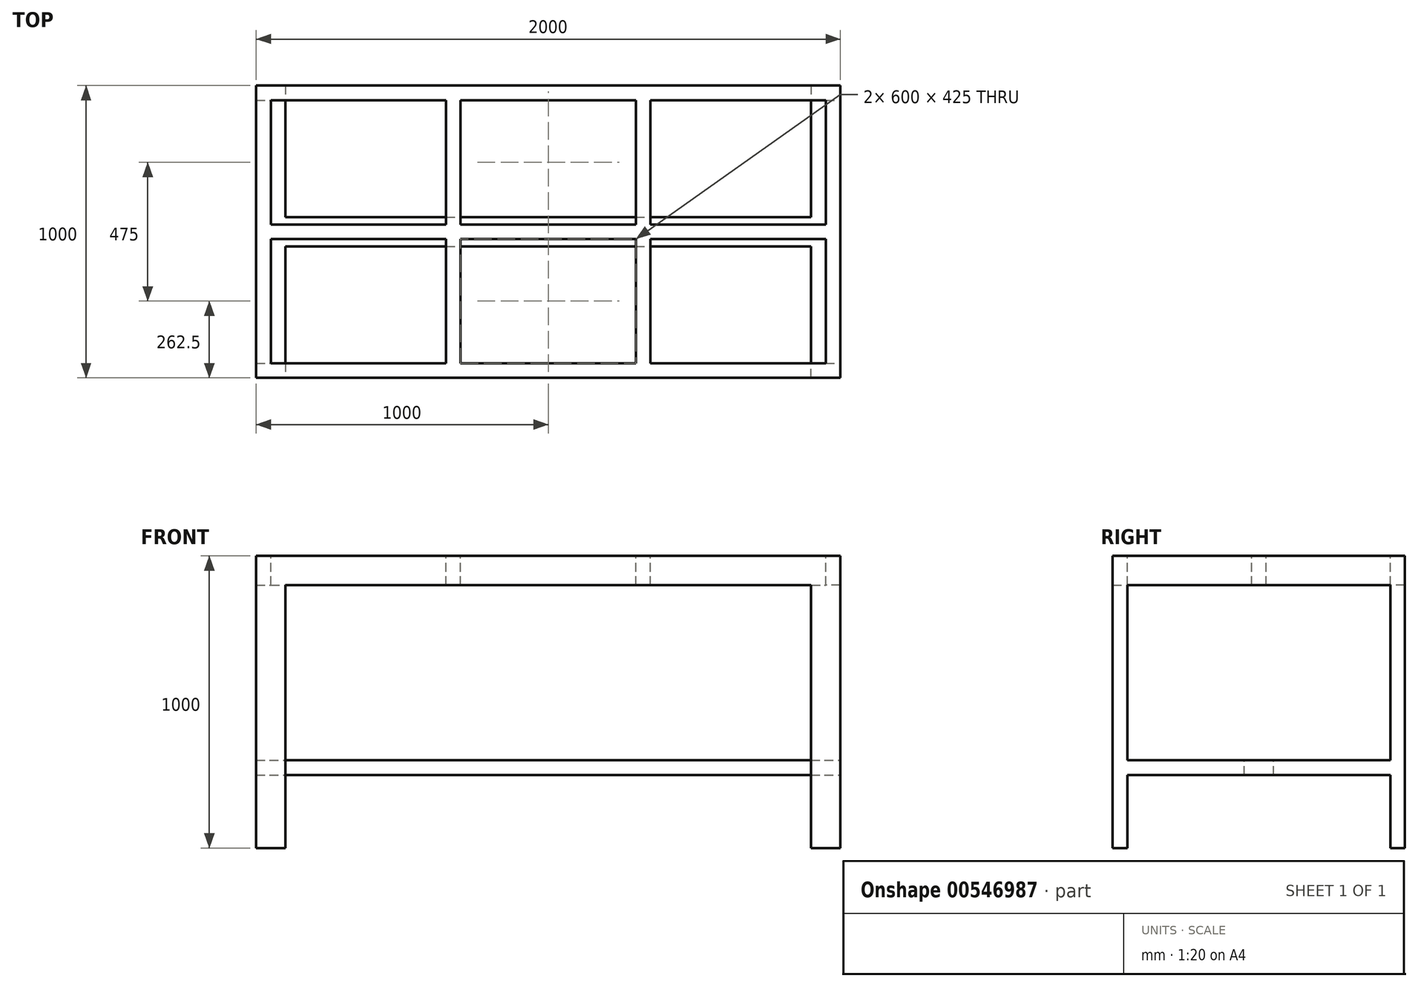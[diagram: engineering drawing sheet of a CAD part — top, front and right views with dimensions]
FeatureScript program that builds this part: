
annotation { "Feature Type Name" : "Feature", "Feature Type Description" : "" }
export const myFeature = defineFeature(function(context is Context, id is Id, definition is map)
    precondition{}
    {
        {
            var Q0;
            Q0=qCreatedBy(makeId("Top.planeOp"),FACE);
            var sketch = newSketch(context, id + "F0", { "sketchPlane" : qUnion([Q0])});
            skLineSegment(sketch, "E0.bottom", {"start": v(-989.4, 627.58) * mm, "end": v(1010.6, 627.58) * mm});
            skLineSegment(sketch, "E0.top", {"start": v(-989.4, -372.42) * mm, "end": v(1010.6, -372.42) * mm});
            skLineSegment(sketch, "E0.left", {"start": v(-989.4, 627.58) * mm, "end": v(-989.4, -372.42) * mm});
            skLineSegment(sketch, "E0.right", {"start": v(1010.6, 627.58) * mm, "end": v(1010.6, -372.42) * mm});
            skSolve(sketch);
        }
        {
            var Q0;
            Q0=makeQuery(id+"F0.imprint","IMPRINT",FACE,{"disambiguationData":[TD([[makeQuery(id+"F0.imprint","IMPRINT",EDGE,{"derivedFrom":sQuery(id+"F0.wireOp",EDGE,"E0.bottom")}),-1.0]])]});
            extrude(context, id + "F1", {"entities" : qUnion([Q0]), "depth" : 100 * mm, "offsetDistance" : 25 * mm});
        }
        {
            var Q0;
            Q0=makeQuery(id+"F1.opExtrude","CAP_FACE",FACE,{"disambiguationData":[OSD([sQuery(id+"F0.wireOp",EDGE,"E0.bottom"),sQuery(id+"F0.wireOp",EDGE,"E0.top"),sQuery(id+"F0.wireOp",EDGE,"E0.left"),sQuery(id+"F0.wireOp",EDGE,"E0.right")])],"isStart":false});
            var sketch = newSketch(context, id + "F2", { "sketchPlane" : qUnion([Q0])});
            skLineSegment(sketch, "E1.bottom", {"start": v(-939.4, 577.58) * mm, "end": v(-339.4, 577.58) * mm});
            skLineSegment(sketch, "E1.top", {"start": v(-939.4, 152.58) * mm, "end": v(-339.4, 152.58) * mm});
            skLineSegment(sketch, "E1.left", {"start": v(-939.4, 577.58) * mm, "end": v(-939.4, 152.58) * mm});
            skLineSegment(sketch, "E1.right", {"start": v(-339.4, 577.58) * mm, "end": v(-339.4, 152.58) * mm});
            skLineSegment(sketch, "E2.bottom", {"start": v(-939.4, 102.58) * mm, "end": v(-339.4, 102.58) * mm});
            skLineSegment(sketch, "E2.top", {"start": v(-939.4, -322.42) * mm, "end": v(-339.4, -322.42) * mm});
            skLineSegment(sketch, "E2.left", {"start": v(-939.4, 102.58) * mm, "end": v(-939.4, -322.42) * mm});
            skLineSegment(sketch, "E2.right", {"start": v(-339.4, 102.58) * mm, "end": v(-339.4, -322.42) * mm});
            skLineSegment(sketch, "E3.bottom", {"start": v(-289.4, 577.58) * mm, "end": v(310.6, 577.58) * mm});
            skLineSegment(sketch, "E3.top", {"start": v(-289.4, 152.58) * mm, "end": v(310.6, 152.58) * mm});
            skLineSegment(sketch, "E3.left", {"start": v(-289.4, 577.58) * mm, "end": v(-289.4, 152.58) * mm});
            skLineSegment(sketch, "E3.right", {"start": v(310.6, 577.58) * mm, "end": v(310.6, 152.58) * mm});
            skLineSegment(sketch, "E4.bottom", {"start": v(360.6, 577.58) * mm, "end": v(960.6, 577.58) * mm});
            skLineSegment(sketch, "E4.top", {"start": v(360.6, 152.58) * mm, "end": v(960.6, 152.58) * mm});
            skLineSegment(sketch, "E4.left", {"start": v(360.6, 577.58) * mm, "end": v(360.6, 152.58) * mm});
            skLineSegment(sketch, "E4.right", {"start": v(960.6, 577.58) * mm, "end": v(960.6, 152.58) * mm});
            skLineSegment(sketch, "E5.top", {"start": v(-289.4, -322.42) * mm, "end": v(310.6, -322.42) * mm});
            skLineSegment(sketch, "E6.bottom", {"start": v(360.6, 102.58) * mm, "end": v(960.6, 102.58) * mm});
            skLineSegment(sketch, "E6.top", {"start": v(360.6, -322.42) * mm, "end": v(960.6, -322.42) * mm});
            skLineSegment(sketch, "E6.left", {"start": v(360.6, 102.58) * mm, "end": v(360.6, -322.42) * mm});
            skLineSegment(sketch, "E6.right", {"start": v(960.6, 102.58) * mm, "end": v(960.6, -322.42) * mm});
            skLineSegment(sketch, "E7", {"start": v(-289.4, -322.42) * mm, "end": v(-289.4, 102.58) * mm});
            skLineSegment(sketch, "E8", {"start": v(-289.4, 102.58) * mm, "end": v(310.6, 102.58) * mm});
            skLineSegment(sketch, "E9", {"start": v(310.6, 102.58) * mm, "end": v(310.6, -322.42) * mm});
            skSolve(sketch);
        }
        {
            var Q0;
            Q0 = qSketchRegion(id + "F2", true);
            extrude(context, id + "F3", {"entities" : qUnion([Q0]), "operationType" : NewBodyOperationType.REMOVE, "oppositeDirection" : true, "depth" : 640 * mm, "offsetDistance" : 25 * mm});
        }
        {
            var Q0;
            Q0=makeQuery(id+"F1.opExtrude","CAP_FACE",FACE,{"disambiguationData":[OSD([sQuery(id+"F0.wireOp",EDGE,"E0.bottom"),sQuery(id+"F0.wireOp",EDGE,"E0.top"),sQuery(id+"F0.wireOp",EDGE,"E0.left"),sQuery(id+"F0.wireOp",EDGE,"E0.right")])],"isStart":false});
            var sketch = newSketch(context, id + "F4", { "sketchPlane" : qUnion([Q0])});
            skLineSegment(sketch, "E10.bottom", {"start": v(910.6, 627.58) * mm, "end": v(1010.6, 627.58) * mm});
            skLineSegment(sketch, "E10.top", {"start": v(910.6, 577.58) * mm, "end": v(1010.6, 577.58) * mm});
            skLineSegment(sketch, "E10.left", {"start": v(910.6, 627.58) * mm, "end": v(910.6, 577.58) * mm});
            skLineSegment(sketch, "E10.right", {"start": v(1010.6, 627.58) * mm, "end": v(1010.6, 577.58) * mm});
            skLineSegment(sketch, "E11.bottom", {"start": v(-989.4, -322.42) * mm, "end": v(-889.4, -322.42) * mm});
            skLineSegment(sketch, "E11.top", {"start": v(-989.4, -372.42) * mm, "end": v(-889.4, -372.42) * mm});
            skLineSegment(sketch, "E11.left", {"start": v(-989.4, -322.42) * mm, "end": v(-989.4, -372.42) * mm});
            skLineSegment(sketch, "E11.right", {"start": v(-889.4, -322.42) * mm, "end": v(-889.4, -372.42) * mm});
            skLineSegment(sketch, "E12.bottom", {"start": v(-989.4, 627.58) * mm, "end": v(-889.4, 627.58) * mm});
            skLineSegment(sketch, "E12.top", {"start": v(-989.4, 577.58) * mm, "end": v(-889.4, 577.58) * mm});
            skLineSegment(sketch, "E12.left", {"start": v(-989.4, 627.58) * mm, "end": v(-989.4, 577.58) * mm});
            skLineSegment(sketch, "E12.right", {"start": v(-889.4, 627.58) * mm, "end": v(-889.4, 577.58) * mm});
            skLineSegment(sketch, "E13.bottom", {"start": v(1010.6, -372.42) * mm, "end": v(910.6, -372.42) * mm});
            skLineSegment(sketch, "E13.top", {"start": v(1010.6, -322.42) * mm, "end": v(910.6, -322.42) * mm});
            skLineSegment(sketch, "E13.left", {"start": v(1010.6, -372.42) * mm, "end": v(1010.6, -322.42) * mm});
            skLineSegment(sketch, "E13.right", {"start": v(910.6, -372.42) * mm, "end": v(910.6, -322.42) * mm});
            skSolve(sketch);
        }
        {
            var Q0;
            Q0 = qSketchRegion(id + "F4", true);
            extrude(context, id + "F5", {"entities" : qUnion([Q0]), "operationType" : NewBodyOperationType.ADD, "oppositeDirection" : true, "depth" : 1000 * mm, "offsetDistance" : 25 * mm});
        }
        {
            var Q0;
            Q0=makeQuery(id+"F5.boolean.opBoolean","MERGE",FACE,{"derivedFrom":[makeQuery(id+"F1.opExtrude","SWEPT_FACE",FACE,{"disambiguationData":[OSD([sQuery(id+"F0.wireOp",EDGE,"E0.top")])]}),makeQuery(id+"F5.opExtrude","SWEPT_FACE",FACE,{"disambiguationData":[OSD([sQuery(id+"F4.wireOp",EDGE,"E11.top")])]}),makeQuery(id+"F5.opExtrude","SWEPT_FACE",FACE,{"disambiguationData":[OSD([sQuery(id+"F4.wireOp",EDGE,"E13.bottom")])]})]});
            var sketch = newSketch(context, id + "F6", { "sketchPlane" : qUnion([Q0])});
            skLineSegment(sketch, "E14.bottom", {"start": v(-989.4, -600) * mm, "end": v(-889.4, -600) * mm});
            skLineSegment(sketch, "E14.top", {"start": v(-989.4, -650) * mm, "end": v(-889.4, -650) * mm});
            skLineSegment(sketch, "E14.left", {"start": v(-989.4, -600) * mm, "end": v(-989.4, -650) * mm});
            skLineSegment(sketch, "E14.right", {"start": v(-889.4, -600) * mm, "end": v(-889.4, -650) * mm});
            skLineSegment(sketch, "E15.bottom", {"start": v(910.6, -600) * mm, "end": v(1010.6, -600) * mm});
            skLineSegment(sketch, "E15.top", {"start": v(910.6, -650) * mm, "end": v(1010.6, -650) * mm});
            skLineSegment(sketch, "E15.left", {"start": v(910.6, -600) * mm, "end": v(910.6, -650) * mm});
            skLineSegment(sketch, "E15.right", {"start": v(1010.6, -600) * mm, "end": v(1010.6, -650) * mm});
            skSolve(sketch);
        }
        {
            var Q0;
            Q0 = qSketchRegion(id + "F6", true);
            extrude(context, id + "F7", {"entities" : qUnion([Q0]), "operationType" : NewBodyOperationType.ADD, "oppositeDirection" : true, "depth" : 1000 * mm, "offsetDistance" : 25 * mm});
        }
        {
            var Q0;
            Q0=makeQuery(id+"F7.boolean.opBoolean","MERGE",FACE,{"derivedFrom":[makeQuery(id+"F5.boolean.opBoolean","MERGE",FACE,{"derivedFrom":[makeQuery(id+"F1.opExtrude","SWEPT_FACE",FACE,{"disambiguationData":[OSD([sQuery(id+"F0.wireOp",EDGE,"E0.right")])]}),makeQuery(id+"F5.opExtrude","SWEPT_FACE",FACE,{"disambiguationData":[OSD([sQuery(id+"F4.wireOp",EDGE,"E10.right")])]}),makeQuery(id+"F5.opExtrude","SWEPT_FACE",FACE,{"disambiguationData":[OSD([sQuery(id+"F4.wireOp",EDGE,"E13.left")])]})]}),makeQuery(id+"F7.opExtrude","SWEPT_FACE",FACE,{"disambiguationData":[OSD([sQuery(id+"F6.wireOp",EDGE,"E15.right")])]})]});
            var sketch = newSketch(context, id + "F8", { "sketchPlane" : qUnion([Q0])});
            skLineSegment(sketch, "E16.bottom", {"start": v(77.58, -600) * mm, "end": v(177.58, -600) * mm});
            skLineSegment(sketch, "E16.top", {"start": v(77.58, -650) * mm, "end": v(177.58, -650) * mm});
            skLineSegment(sketch, "E16.left", {"start": v(77.58, -600) * mm, "end": v(77.58, -650) * mm});
            skLineSegment(sketch, "E16.right", {"start": v(177.58, -600) * mm, "end": v(177.58, -650) * mm});
            skSolve(sketch);
        }
        {
            var Q0;
            Q0 = qSketchRegion(id + "F8", true);
            extrude(context, id + "F9", {"entities" : qUnion([Q0]), "operationType" : NewBodyOperationType.ADD, "oppositeDirection" : true, "depth" : 2000 * mm, "offsetDistance" : 25 * mm});
        }
    });
